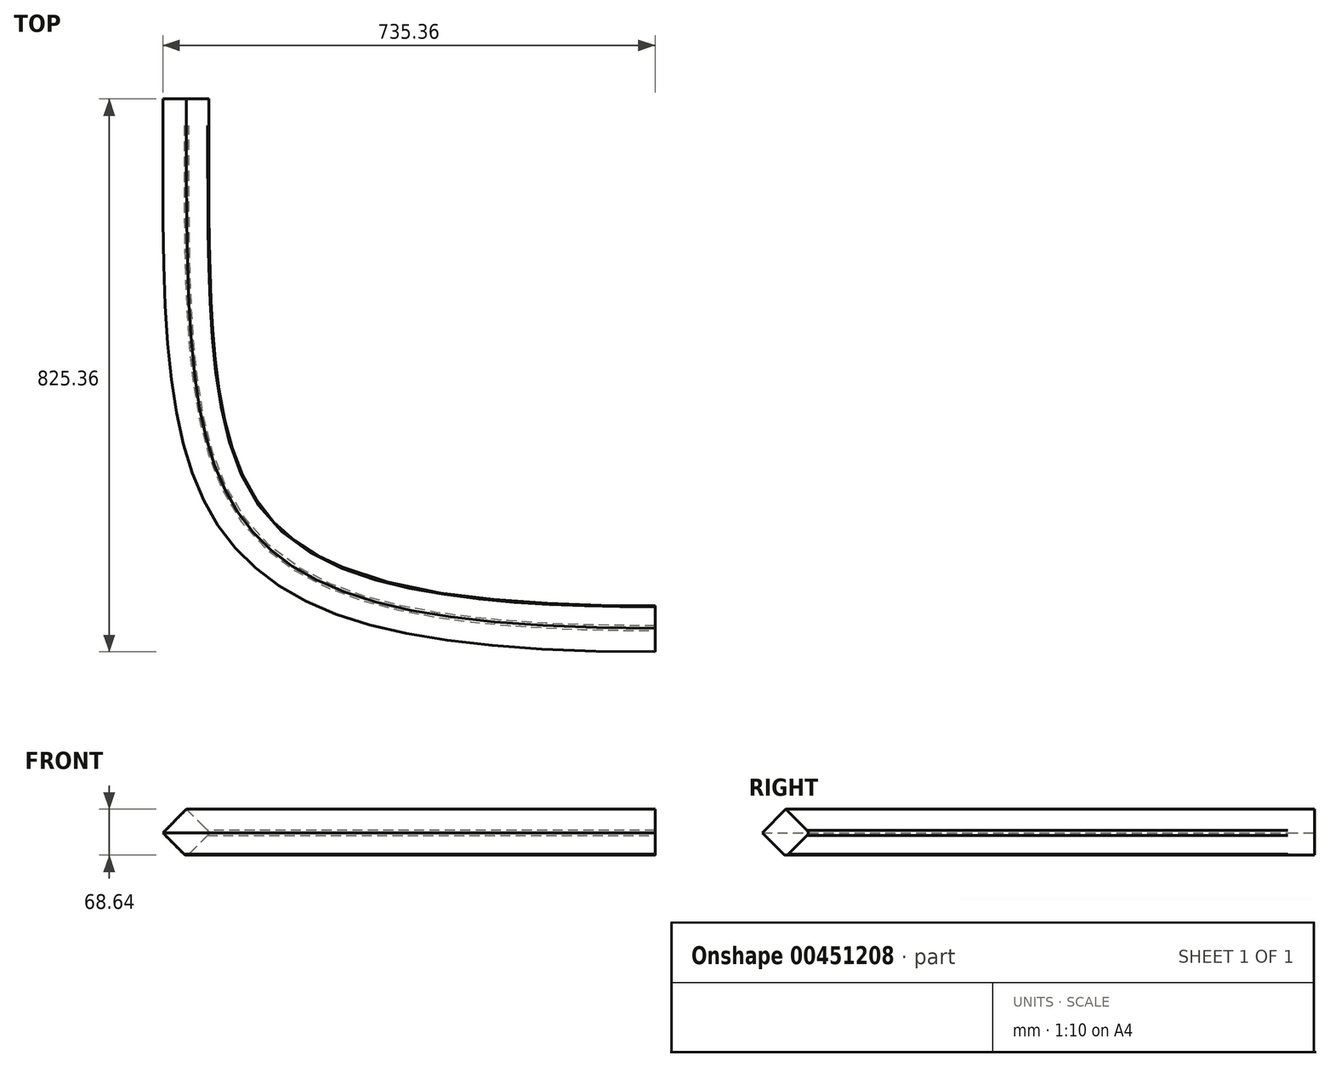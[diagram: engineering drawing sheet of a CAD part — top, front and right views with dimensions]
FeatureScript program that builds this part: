
annotation { "Feature Type Name" : "Feature", "Feature Type Description" : "" }
export const myFeature = defineFeature(function(context is Context, id is Id, definition is map)
    precondition{}
    {
        {
            var Q0;
            Q0=qCreatedBy(makeId("Right.planeOp"),FACE);
            cPlane(context, id + "F0", {"entities" : qUnion([Q0]), "cplaneType" : CPlaneType.OFFSET, "offset" : 0 * mm, "oppositeDirection" : true, "width" : 150 * mm, "height" : 150 * mm});
        }
        {
            var Q0;
            Q0=qCreatedBy(id+"F0.planeOp",FACE);
            var sketch = newSketch(context, id + "F1", { "sketchPlane" : qUnion([Q0])});
            skLineSegment(sketch, "E0.bottom", {"start": v(-35.36, -8.44) * mm, "end": v(0, -43.8) * mm});
            skLineSegment(sketch, "E0.top", {"start": v(0, 26.91) * mm, "end": v(35.36, -8.44) * mm});
            skLineSegment(sketch, "E0.left", {"start": v(-35.36, -8.44) * mm, "end": v(0, 26.91) * mm});
            skLineSegment(sketch, "E0.right", {"start": v(0, -43.8) * mm, "end": v(35.36, -8.44) * mm});
            skPoint(sketch, "E0.middle", {"position": v(0, -8.44) * mm});
            skSolve(sketch);
        }
        {
            var Q0;
            Q0=qCreatedBy(makeId("Front.planeOp"),FACE);
            cPlane(context, id + "F2", {"entities" : qUnion([Q0]), "cplaneType" : CPlaneType.OFFSET, "offset" : 562 * mm, "oppositeDirection" : true, "width" : 150 * mm, "height" : 150 * mm});
        }
        {
            var Q0;
            Q0=qCreatedBy(makeId("Top.planeOp"),FACE);
            var sketch = newSketch(context, id + "F3", { "sketchPlane" : qUnion([Q0])});
            skFitSpline(sketch, "E1", {"points": [v(0, 0) * mm, v(-700, 750) * mm], "startDerivative": vector(-2100.54, 0) * mm, "endDerivative": vector(0, 1738.56) * mm});
            skLineSegment(sketch, "E2", {"start": v(-700, 750) * mm, "end": v(-700, 800) * mm});
            skSolve(sketch);
        }
        {
            var Q0;
            Q0=makeQuery(id+"F1.imprint","IMPRINT",FACE,{"disambiguationData":[TD([[makeQuery(id+"F1.imprint","IMPRINT",EDGE,{"derivedFrom":sQuery(id+"F1.wireOp",EDGE,"E0.bottom")}),1.0]])]});
            var Q1;
            Q1 = qConstructionFilter(qBodyType(qCreatedBy(id + "F3" ,EDGE), BodyType.WIRE), ConstructionObject.NO);
            sweep(context, id + "F4", {"profiles" : qUnion([Q0]), "path" : qUnion([Q1])});
        }
        {
            var Q0;
            Q0=makeQuery(id+"F4.opSweep","SWEPT_EDGE",EDGE,{"disambiguationData":[OSD([sQuery(id+"F1.wireOp",EDGE,"E0.top"),sQuery(id+"F1.wireOp",EDGE,"E0.right"),sQuery(id+"F3.wireOp",EDGE,"E1")])]});
            var Q1;
            Q1=makeQuery(id+"F4.opSweep","SWEPT_EDGE",EDGE,{"disambiguationData":[OSD([sQuery(id+"F1.wireOp",EDGE,"E0.bottom"),sQuery(id+"F1.wireOp",EDGE,"E0.right"),sQuery(id+"F3.wireOp",EDGE,"E1")])]});
            fillet(context, id + "F5", {"entities" : qUnion([Q0, Q1]), "radius" : 5 * mm, "tangentPropagation" : true, "allowEdgeOverflow" : false});
        }
        {
            var Q0;
            Q0=qCreatedBy(makeId("Top.planeOp"),FACE);
            var sketch = newSketch(context, id + "F6", { "sketchPlane" : qUnion([Q0])});
            skLineSegment(sketch, "E3.bottom", {"start": v(-1017.32, 903.54) * mm, "end": v(-447.36, 903.54) * mm});
            skLineSegment(sketch, "E3.top", {"start": v(-1017.32, 790) * mm, "end": v(-447.36, 790) * mm});
            skLineSegment(sketch, "E3.left", {"start": v(-1017.32, 903.54) * mm, "end": v(-1017.32, 790) * mm});
            skLineSegment(sketch, "E3.right", {"start": v(-447.36, 903.54) * mm, "end": v(-447.36, 790) * mm});
            skSolve(sketch);
        }
        {
            var Q0;
            Q0 = qSketchRegion(id + "F6", true);
            extrude(context, id + "F7", {"entities" : qUnion([Q0]), "operationType" : NewBodyOperationType.REMOVE, "oppositeDirection" : true, "depth" : 109 * mm, "offsetDistance" : 25 * mm, "symmetric" : true});
        }
    });
